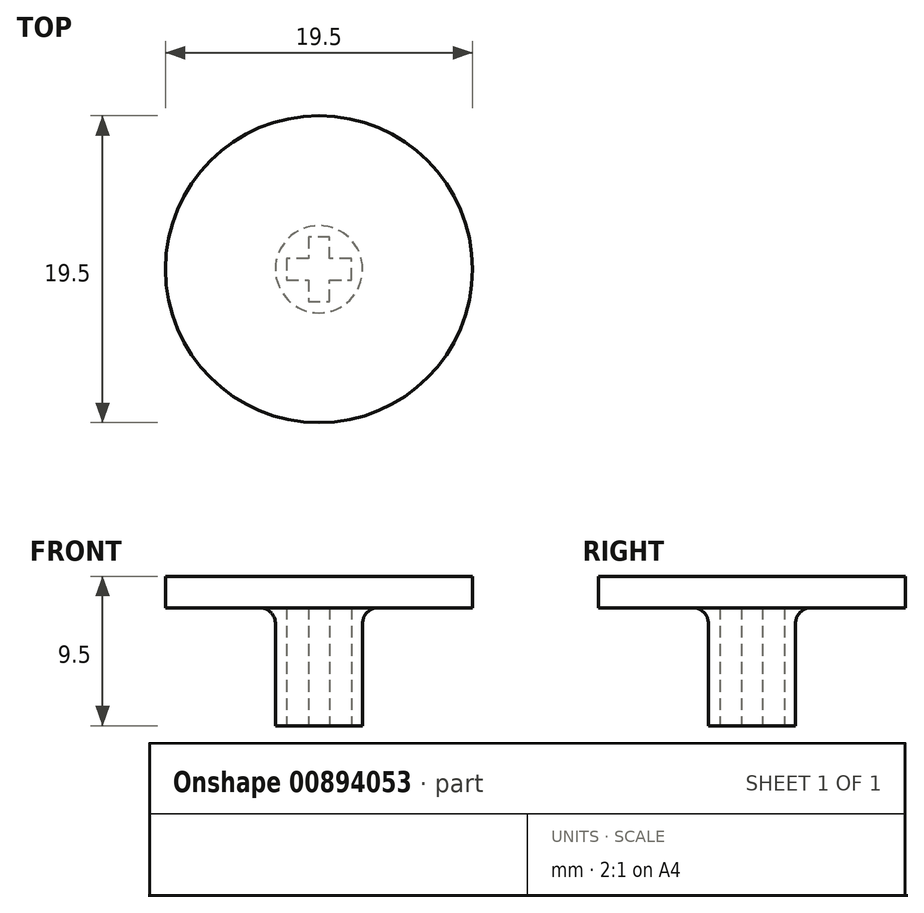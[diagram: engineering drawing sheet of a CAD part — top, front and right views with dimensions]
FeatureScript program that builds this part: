
annotation { "Feature Type Name" : "Feature", "Feature Type Description" : "" }
export const myFeature = defineFeature(function(context is Context, id is Id, definition is map)
    precondition{}
    {
        {
            var Q0;
            Q0=qCreatedBy(makeId("Front.planeOp"),FACE);
            var sketch = newSketch(context, id + "F0", { "sketchPlane" : qUnion([Q0])});
            skLineSegment(sketch, "E0.bottom", {"start": v(0, 0) * mm, "end": v(2.77, 0) * mm});
            skLineSegment(sketch, "E0.top", {"start": v(0, 7.5) * mm, "end": v(2.77, 7.5) * mm});
            skLineSegment(sketch, "E0.left", {"start": v(0, 0) * mm, "end": v(0, 7.5) * mm});
            skLineSegment(sketch, "E0.right", {"start": v(2.77, 0) * mm, "end": v(2.77, 7.5) * mm});
            skLineSegment(sketch, "E1.bottom", {"start": v(0, 7.5) * mm, "end": v(9.75, 7.5) * mm});
            skLineSegment(sketch, "E1.top", {"start": v(0, 9.5) * mm, "end": v(9.75, 9.5) * mm});
            skLineSegment(sketch, "E1.left", {"start": v(0, 7.5) * mm, "end": v(0, 9.5) * mm});
            skLineSegment(sketch, "E1.right", {"start": v(9.75, 7.5) * mm, "end": v(9.75, 9.5) * mm});
            skSolve(sketch);
        }
        {
            var Q0;
            Q0=makeQuery(id+"F0.imprint","IMPRINT",FACE,{"disambiguationData":[TD([[makeQuery(id+"F0.imprint","IMPRINT",EDGE,{"derivedFrom":sQuery(id+"F0.wireOp",EDGE,"E1.top")}),-1.0]])]});
            var Q1;
            Q1=makeQuery(id+"F0.imprint","IMPRINT",FACE,{"disambiguationData":[TD([[makeQuery(id+"F0.imprint","IMPRINT",EDGE,{"derivedFrom":sQuery(id+"F0.wireOp",EDGE,"E0.bottom")}),1.0]])]});
            var Q2;
            Q2=sQuery(id+"F0.wireOp",EDGE,"E0.left");
            revolve(context, id + "F1", {"surfaceOperationType" : NewSurfaceOperationType.NEW, "entities" : qUnion([Q0, Q1]), "axis" : qUnion([Q2]), "revolveType" : RevolveType.FULL});
        }
        {
            var Q0;
            Q0=makeQuery(id+"F1.opRevolve","SWEPT_FACE",FACE,{"disambiguationData":[OSD([sQuery(id+"F0.wireOp",EDGE,"E0.bottom")])]});
            var sketch = newSketch(context, id + "F2", { "sketchPlane" : qUnion([Q0])});
            skLineSegment(sketch, "E2", {"start": v(-0.68, 2.05) * mm, "end": v(0.67, 2.05) * mm});
            skLineSegment(sketch, "E3", {"start": v(0.67, 2.05) * mm, "end": v(0.68, 0.67) * mm});
            skLineSegment(sketch, "E4", {"start": v(0.68, 0.67) * mm, "end": v(2.05, 0.68) * mm});
            skLineSegment(sketch, "E5", {"start": v(2.05, 0.68) * mm, "end": v(2.05, -0.67) * mm});
            skLineSegment(sketch, "E6", {"start": v(2.05, -0.67) * mm, "end": v(0.68, -0.67) * mm});
            skLineSegment(sketch, "E7", {"start": v(0.68, -0.67) * mm, "end": v(0.68, -2.05) * mm});
            skLineSegment(sketch, "E8", {"start": v(0.68, -2.05) * mm, "end": v(-0.67, -2.05) * mm});
            skLineSegment(sketch, "E9", {"start": v(-0.67, -2.05) * mm, "end": v(-0.67, -0.67) * mm});
            skLineSegment(sketch, "E10", {"start": v(-0.67, -0.67) * mm, "end": v(-2.05, -0.68) * mm});
            skLineSegment(sketch, "E11", {"start": v(-2.05, -0.68) * mm, "end": v(-2.05, 0.67) * mm});
            skLineSegment(sketch, "E12", {"start": v(-2.05, 0.67) * mm, "end": v(-0.67, 0.67) * mm});
            skLineSegment(sketch, "E13", {"start": v(-0.68, 0.67) * mm, "end": v(-0.68, 2.05) * mm});
            skSolve(sketch);
        }
        {
            var Q0;
            Q0=makeQuery(id+"F2.imprint","IMPRINT",FACE,{"disambiguationData":[TD([[makeQuery(id+"F2.imprint","IMPRINT",EDGE,{"derivedFrom":sQuery(id+"F2.wireOp",EDGE,"E2")}),-1.0]])]});
            extrude(context, id + "F3", {"entities" : qUnion([Q0]), "operationType" : NewBodyOperationType.REMOVE, "oppositeDirection" : true, "depth" : 7.5 * mm, "offsetDistance" : 25 * mm});
        }
        {
            var Q0;
            Q0=makeQuery(id+"F1.opRevolve","SWEPT_EDGE",EDGE,{"disambiguationData":[OSD([sQuery(id+"F0.wireOp",EDGE,"E0.right"),sQuery(id+"F0.wireOp",EDGE,"E1.bottom")])]});
            fillet(context, id + "F4", {"entities" : qUnion([Q0]), "radius" : 1 * mm, "tangentPropagation" : true, "allowEdgeOverflow" : false});
        }
    });
